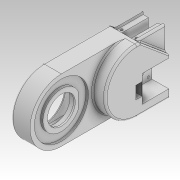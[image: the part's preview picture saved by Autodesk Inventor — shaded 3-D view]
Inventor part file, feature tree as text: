
AUTODESK INVENTOR PART (.ipt)
format: ipt  version: 2020 (Build 240168000, 168)  size: 791,552 bytes
history: native  units: mm
features: sketch x32, extrude x30, chamfer x4, fillet x3, plane x2, revolve x2, projected_geometry x1
ambient origin geometry x8: Origin, YZ Plane, XZ Plane, XY Plane, X Axis, Y Axis, Z Axis, Center Point
bodies: Solid1 (feature_tree)
feature tree (74):
  extrude  "Extrusion1"  Depth=250.0mm
  extrude  "Extrusion3"  Depth=50.0mm TaperAngle=0.0deg
  extrude  "Extrusion6"  TaperAngle=0.0deg  [1 undecoded]
  extrude  "Extrusion7"  Depth=8.726646mm
  extrude  "Extrusion8"  Depth=10.0mm TaperAngle=0.0deg
  extrude  "Extrusion9"  TaperAngle=0.0deg  [1 undecoded]
  extrude  "Extrusion10"  TaperAngle=30.0deg  [1 undecoded]
  extrude  "Extrusion11"  Depth=16.15mm
  extrude  "Extrusion12"  Depth=60.0mm
  plane  "Work Plane1"
  extrude  "Extrusion13"  Depth=10.0mm TaperAngle=0.0deg
  revolve  "Revolution1"  [1 undecoded]
  extrude  "Extrusion14"  Depth=86.0mm
  extrude  "Extrusion15"  Depth=4.0mm TaperAngle=0.0deg
  extrude  "Extrusion16"  Depth=75.0mm
  revolve  "Revolution2"  [1 undecoded]
  extrude  "Extrusion17"  Depth=7.3mm
  fillet  "Fillet1"  [1 undecoded]
  plane  "Work Plane2"
  extrude  "Extrusion18"  Depth=31.0mm
  extrude  "Extrusion19"  Depth=3.0mm TaperAngle=0.0deg
  extrude  "Extrusion20"  Depth=15.0mm TaperAngle=0.0deg
  extrude  "Extrusion21"  Depth=15.0mm
  extrude  "Extrusion25"  Depth=80.0mm TaperAngle=360.0deg
  extrude  "Extrusion22"  Depth=15.0mm
  fillet  "Fillet2"  Radius=5.2mm
  fillet  "Fillet3"  Radius=1.0mm
  extrude  "Extrusion23"  TaperAngle=90.0deg  [1 undecoded]
  extrude  "Extrusion24"  Depth=20.0mm
  extrude  "Extrusion26"  Depth=19.198622mm
  extrude  "Extrusion27"  Depth=15.0mm
  extrude  "Extrusion28"  TaperAngle=0.0deg  [1 undecoded]
  extrude  "CHOP"  Depth=8.0mm
  extrude  "Extrusion30"  Depth=12.5mm
  extrude  "Extrusion31"  Depth=2.45mm
  extrude  "Extrusion32"  Depth=10.0mm
  chamfer  "Chamfer1"  Distance=110.0mm
  chamfer  "Chamfer2"  Distance=3.0mm
  chamfer  "Chamfer3"  Distance=3.0mm
  chamfer  "Chamfer4"  Distance=5.0mm
  extrude  "Extrusion33"  Depth=0.2mm
  sketch  "Sketch1"  dims[d0=50.0mm d1=250.0mm]
  sketch  "Sketch3"  dims[d2=47.2mm d3=50.0mm d4=0.0mm]
  sketch  "Sketch6"  dims[d10=5.0mm d11=0.0mm d12=0.0mm]
  sketch  "Sketch7"  dims[d19=50.0mm d20=0.0mm d21=8.726646mm]
  projected_geometry  "Projected Loop1"
  sketch  "Sketch8"  dims[d22=75.0mm d25=10.0mm d26=0.0mm]
  sketch  "Sketch9"  dims[d27=50.0mm d30=0.0mm d31=0.0mm]
  sketch  "Sketch10"  dims[d33=30.0deg d34=30.0deg]
  sketch  "Sketch11"  dims[d35=0.0mm d36=0.0mm d37=16.15mm]
  sketch  "Sketch12"  dims[d38=3.3mm d39=60.0mm]
  sketch  "Sketch13"  dims[d40=80.0mm d42=360.0deg d44=10.0mm d45=0.0mm]
  sketch  "Sketch14"  dims[d50=42.5mm d51=42.5mm d52=0.0mm d53=0.0mm]
  sketch  "Sketch15"  dims[d54=38.0mm d55=86.0mm]
  sketch  "Sketch16"  dims[d56=59.0mm d57=4.0mm d58=0.0mm]
  sketch  "Sketch17"  dims[d59=-2.0mm d60=75.0mm]
  sketch  "Sketch18"  dims[d61=40.0mm d62=18.0mm d63=0.0mm]
  sketch  "Sketch19"  dims[d64=1.5mm d65=7.3mm d66=90.0deg]
  sketch  "Sketch20"  dims[d67=22.0mm d68=31.0mm]
  sketch  "Sketch21"  dims[d69=3.5mm d70=3.0mm d71=0.0mm]
  sketch  "Sketch22"  dims[d72=0.0mm d73=15.0mm d74=0.0mm]
  sketch  "Sketch23"  dims[d75=15.0mm d76=130.0mm]
  sketch  "Sketch24"  dims[d77=6.0mm d78=80.0mm d80=360.0deg]
  sketch  "Sketch25"  dims[d82=15.0mm d83=0.0mm d84=5.2mm d85=5.2mm d86=1.0mm]
  sketch  "Sketch26"  dims[d87=1.5mm d88=90.0deg]
  sketch  "Sketch27"  dims[d89=5.5mm d90=20.0mm]
  sketch  "Sketch28"  dims[d91=30.0deg d92=19.198622mm]
  sketch  "Sketch29"  dims[d93=15.0mm d94=0.0mm d95=50.0mm]
  sketch  "Sketch30"  dims[d96=30.0mm d97=0.0mm]
  sketch  "Sketch31"  dims[d98=8.0mm d99=14.0mm]
  sketch  "Sketch32"  dims[d100=6.4mm d101=12.5mm]
  sketch  "Sketch33"  dims[d102=130.0mm d103=80.0mm d104=0.0mm d105=0.0mm d106=2.45mm]
  sketch  "Sketch34"  dims[d107=10.0mm d108=10.0mm]
  sketch  "Sketch35"  dims[d109=32.0mm d110=110.0mm d111=0.0mm d112=3.0mm d113=3.0mm d114=5.0mm d115=1.0mm d116=4.0mm d117=0.0mm d118=4.0mm d119=4.0mm d120=32.25mm d121=0.0mm d122=3.0mm d124=0.5mm d125=0.0mm d126=3.0mm d127=2.0mm d128=8.0mm d129=8.0mm d130=4.0mm d131=4.0mm d132=3.9mm d133=6.0mm d134=0.0mm d135=4.0mm d136=0.0mm d137=70.0mm d138=0.5mm d139=0.0mm d140=2.5mm d141=10.0mm d142=20.0mm d143=15.0mm d144=0.0mm d145=8.0mm d146=23.75mm d147=0.0mm d148=15.0mm d149=23.75mm d150=0.0mm d151=200.998mm d152=0.0mm d153=0.0mm d154=0.0mm d155=5.0mm d156=2.0mm d157=45.0deg d158=10.0mm d159=3.5mm d160=0.0mm d161=0.8mm d162=2.0mm d163=45.0deg d164=6.108652mm d165=37.0mm d166=0.0mm d167=0.5mm d168=2.0mm d169=45.0deg d170=10.0mm d171=2.0mm d172=45.0deg d173=0.2mm d174=0.0mm d123=0.872665mm]
note: 8 required parameter values undecoded (feature->parameter linkage not recoverable at this tier; creation-order binding heuristic only, values carry confidence <= 0.55)